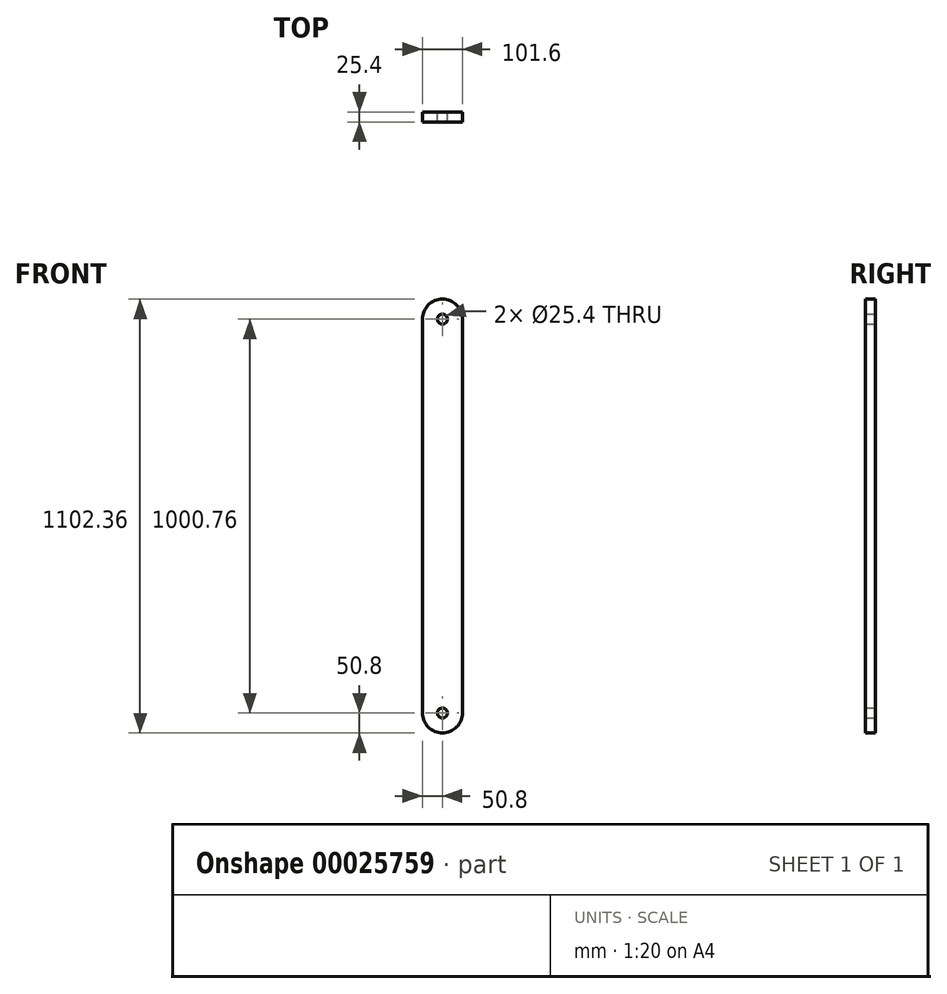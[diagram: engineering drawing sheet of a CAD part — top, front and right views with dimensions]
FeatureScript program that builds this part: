
annotation { "Feature Type Name" : "Feature", "Feature Type Description" : "" }
export const myFeature = defineFeature(function(context is Context, id is Id, definition is map)
    precondition{}
    {
        {
            var Q0;
            Q0=qCreatedBy(makeId("Front.planeOp"),FACE);
            var sketch = newSketch(context, id + "F0", { "sketchPlane" : qUnion([Q0])});
            skCircle(sketch, "E0", {"center": v(0, 0) * mm, "radius": 12.7 * mm});
            skLineSegment(sketch, "E1", {"start": v(50.8, 0) * mm, "end": v(50.8, 1000.76) * mm});
            skLineSegment(sketch, "E2", {"start": v(-50.8, 0) * mm, "end": v(-50.8, 1000.76) * mm});
            skArc(sketch, "E3", {"start": v(-50.8, 0) * mm, "mid": v(0, -50.8) * mm, "end": v(50.8, 0) * mm});
            skArc(sketch, "E4", {"start": v(50.8, 1000.76) * mm, "mid": v(0, 1051.56) * mm, "end": v(-50.8, 1000.76) * mm});
            skCircle(sketch, "E5", {"center": v(0, 1000.76) * mm, "radius": 12.7 * mm});
            skSolve(sketch);
        }
        {
            var Q0;
            Q0 = qSketchRegion(id + "F0", true);
            extrude(context, id + "F1", {"entities" : qUnion([Q0]), "depth" : 25.4 * mm});
        }
    });
